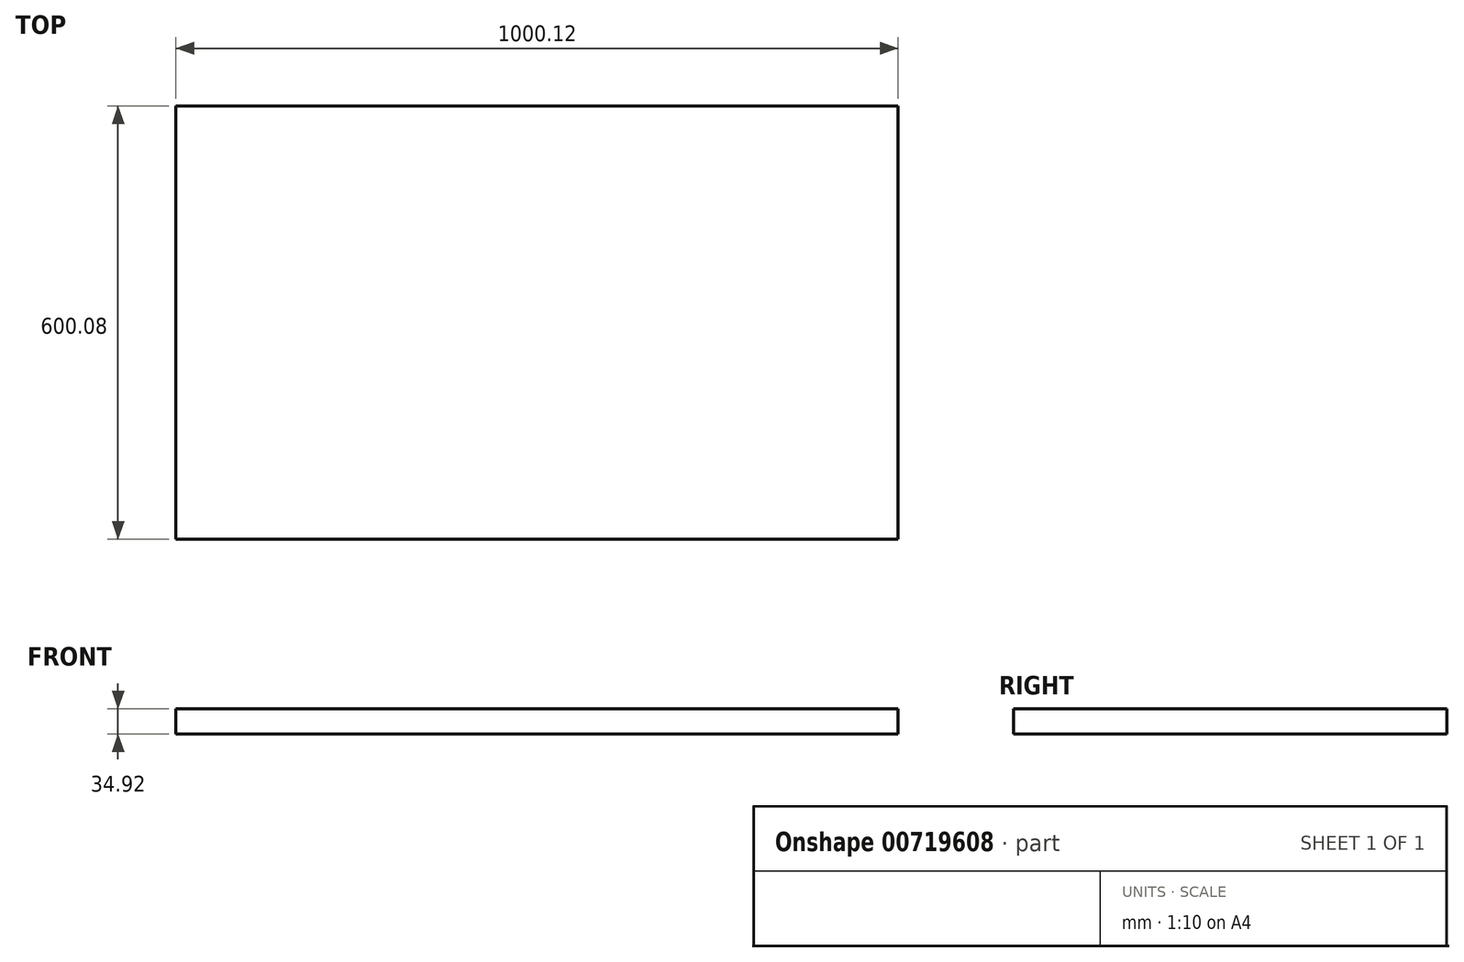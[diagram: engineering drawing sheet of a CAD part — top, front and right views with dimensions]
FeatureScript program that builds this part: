
annotation { "Feature Type Name" : "Feature", "Feature Type Description" : "" }
export const myFeature = defineFeature(function(context is Context, id is Id, definition is map)
    precondition{}
    {
        {
            var Q0;
            Q0=qCreatedBy(makeId("Top.planeOp"),FACE);
            var sketch = newSketch(context, id + "F0", { "sketchPlane" : qUnion([Q0])});
            skLineSegment(sketch, "E0.bottom", {"start": v(0, 0) * mm, "end": v(1000.13, 0) * mm});
            skLineSegment(sketch, "E0.top", {"start": v(0, 600.07) * mm, "end": v(1000.13, 600.07) * mm});
            skLineSegment(sketch, "E0.left", {"start": v(0, 0) * mm, "end": v(0, 600.07) * mm});
            skLineSegment(sketch, "E0.right", {"start": v(1000.13, 0) * mm, "end": v(1000.13, 600.08) * mm});
            skSolve(sketch);
        }
        {
            var Q0;
            Q0=makeQuery(id+"F0.imprint","IMPRINT",FACE,{"disambiguationData":[TD([[makeQuery(id+"F0.imprint","IMPRINT",EDGE,{"derivedFrom":sQuery(id+"F0.wireOp",EDGE,"E0.bottom")}),1.0]])]});
            extrude(context, id + "F1", {"entities" : qUnion([Q0]), "oppositeDirection" : true, "depth" : 34.92 * mm, "offsetDistance" : 25.4 * mm});
        }
    });
